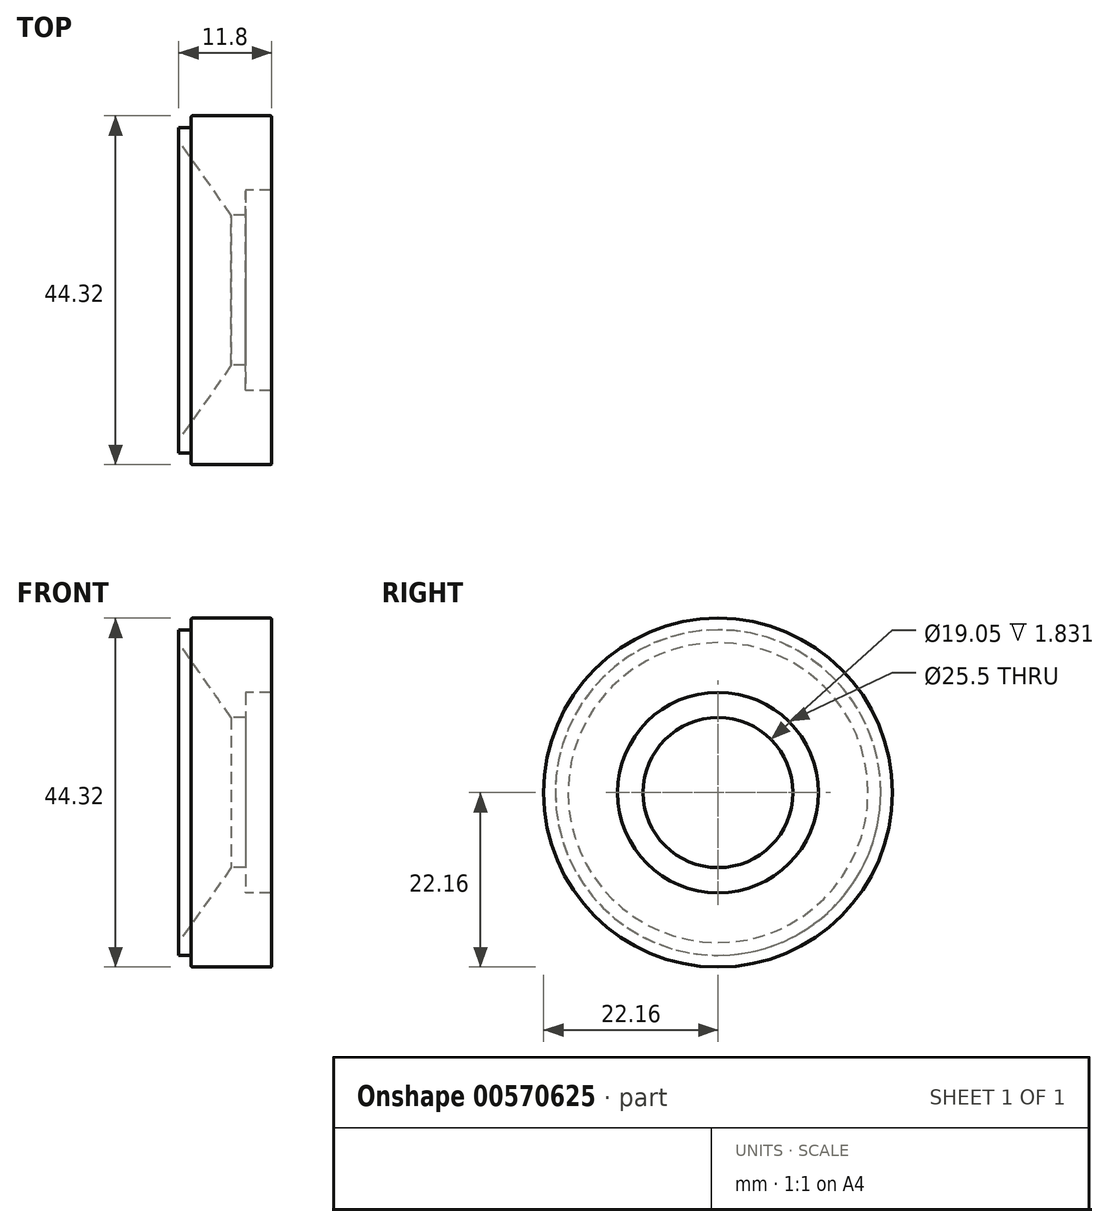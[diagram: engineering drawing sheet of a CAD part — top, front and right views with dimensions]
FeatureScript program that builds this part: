
annotation { "Feature Type Name" : "Feature", "Feature Type Description" : "" }
export const myFeature = defineFeature(function(context is Context, id is Id, definition is map)
    precondition{}
    {
        {
            var Q0;
            Q0=qCreatedBy(makeId("Top.planeOp"),FACE);
            var sketch = newSketch(context, id + "F0", { "sketchPlane" : qUnion([Q0])});
            skLineSegment(sketch, "E0", {"start": v(-8.63, 0) * mm, "end": v(17.46, 0) * mm, "construction": true});
            skLineSegment(sketch, "E1", {"start": v(11.8, 22.16) * mm, "end": v(1.6, 22.16) * mm});
            skLineSegment(sketch, "E2", {"start": v(0, 20.68) * mm, "end": v(0, 19.05) * mm});
            skLineSegment(sketch, "E3", {"start": v(0, 19.05) * mm, "end": v(6.67, 9.52) * mm});
            skLineSegment(sketch, "E4", {"start": v(6.67, 9.53) * mm, "end": v(8.5, 9.53) * mm});
            skLineSegment(sketch, "E5", {"start": v(8.5, 9.53) * mm, "end": v(8.5, 12.75) * mm});
            skLineSegment(sketch, "E6", {"start": v(8.5, 12.75) * mm, "end": v(11.8, 12.75) * mm});
            skLineSegment(sketch, "E7", {"start": v(11.8, 12.75) * mm, "end": v(11.8, 22.16) * mm});
            skLineSegment(sketch, "E8.MirrorCS", {"start": v(8.5, -9.53) * mm, "end": v(8.5, -12.75) * mm});
            skLineSegment(sketch, "E9.MirrorCS", {"start": v(6.67, -9.53) * mm, "end": v(8.5, -9.53) * mm});
            skLineSegment(sketch, "E10.MirrorCS", {"start": v(11.8, -12.75) * mm, "end": v(11.8, -22.16) * mm});
            skLineSegment(sketch, "E11.MirrorCS", {"start": v(0, -19.05) * mm, "end": v(6.67, -9.53) * mm});
            skLineSegment(sketch, "E12.MirrorCS", {"start": v(8.5, -12.75) * mm, "end": v(11.8, -12.75) * mm});
            skLineSegment(sketch, "E13.top", {"start": v(0, 20.68) * mm, "end": v(1.6, 20.68) * mm});
            skLineSegment(sketch, "E13.right", {"start": v(1.6, 22.16) * mm, "end": v(1.6, 20.68) * mm});
            skLineSegment(sketch, "E14.MirrorCS", {"start": v(0, -20.68) * mm, "end": v(0, -19.05) * mm});
            skLineSegment(sketch, "E15.MirrorCS", {"start": v(0, -20.68) * mm, "end": v(1.6, -20.68) * mm});
            skLineSegment(sketch, "E16.MirrorCS", {"start": v(11.8, -22.16) * mm, "end": v(1.6, -22.16) * mm});
            skLineSegment(sketch, "E17.MirrorCS", {"start": v(1.6, -22.16) * mm, "end": v(1.6, -20.68) * mm});
            skSolve(sketch);
        }
        {
            var Q0;
            Q0=makeQuery(id+"F0.imprint","IMPRINT",FACE,{"disambiguationData":[TD([[makeQuery(id+"F0.imprint","IMPRINT",EDGE,{"derivedFrom":sQuery(id+"F0.wireOp",EDGE,"E1")}),1.0]])]});
            var Q1;
            Q1=sQuery(id+"F0.wireOp",EDGE,"E0");
            revolve(context, id + "F1", {"entities" : qUnion([Q0]), "axis" : qUnion([Q1]), "revolveType" : RevolveType.FULL});
        }
        {
            var Q0;
            Q0=makeQuery(id+"F1.opRevolve","SWEPT_EDGE",EDGE,{"disambiguationData":[OSD([sQuery(id+"F0.wireOp",EDGE,"E13.top"),sQuery(id+"F0.wireOp",EDGE,"E13.right")])]});
            var Q1;
            Q1=makeQuery(id+"F1.opRevolve","SWEPT_EDGE",EDGE,{"disambiguationData":[OSD([sQuery(id+"F0.wireOp",EDGE,"E5"),sQuery(id+"F0.wireOp",EDGE,"E6")])]});
            var Q2;
            Q2=makeQuery(id+"F1.opRevolve","SWEPT_EDGE",EDGE,{"disambiguationData":[OSD([sQuery(id+"F0.wireOp",EDGE,"E1"),sQuery(id+"F0.wireOp",EDGE,"E7")])]});
            var Q3;
            Q3=makeQuery(id+"F1.opRevolve","SWEPT_EDGE",EDGE,{"disambiguationData":[OSD([sQuery(id+"F0.wireOp",EDGE,"E1"),sQuery(id+"F0.wireOp",EDGE,"E13.right")])]});
            fillet(context, id + "F2", {"entities" : qUnion([Q0, Q1, Q2, Q3]), "radius" : 0.13 * mm, "tangentPropagation" : true, "allowEdgeOverflow" : false});
        }
    });
